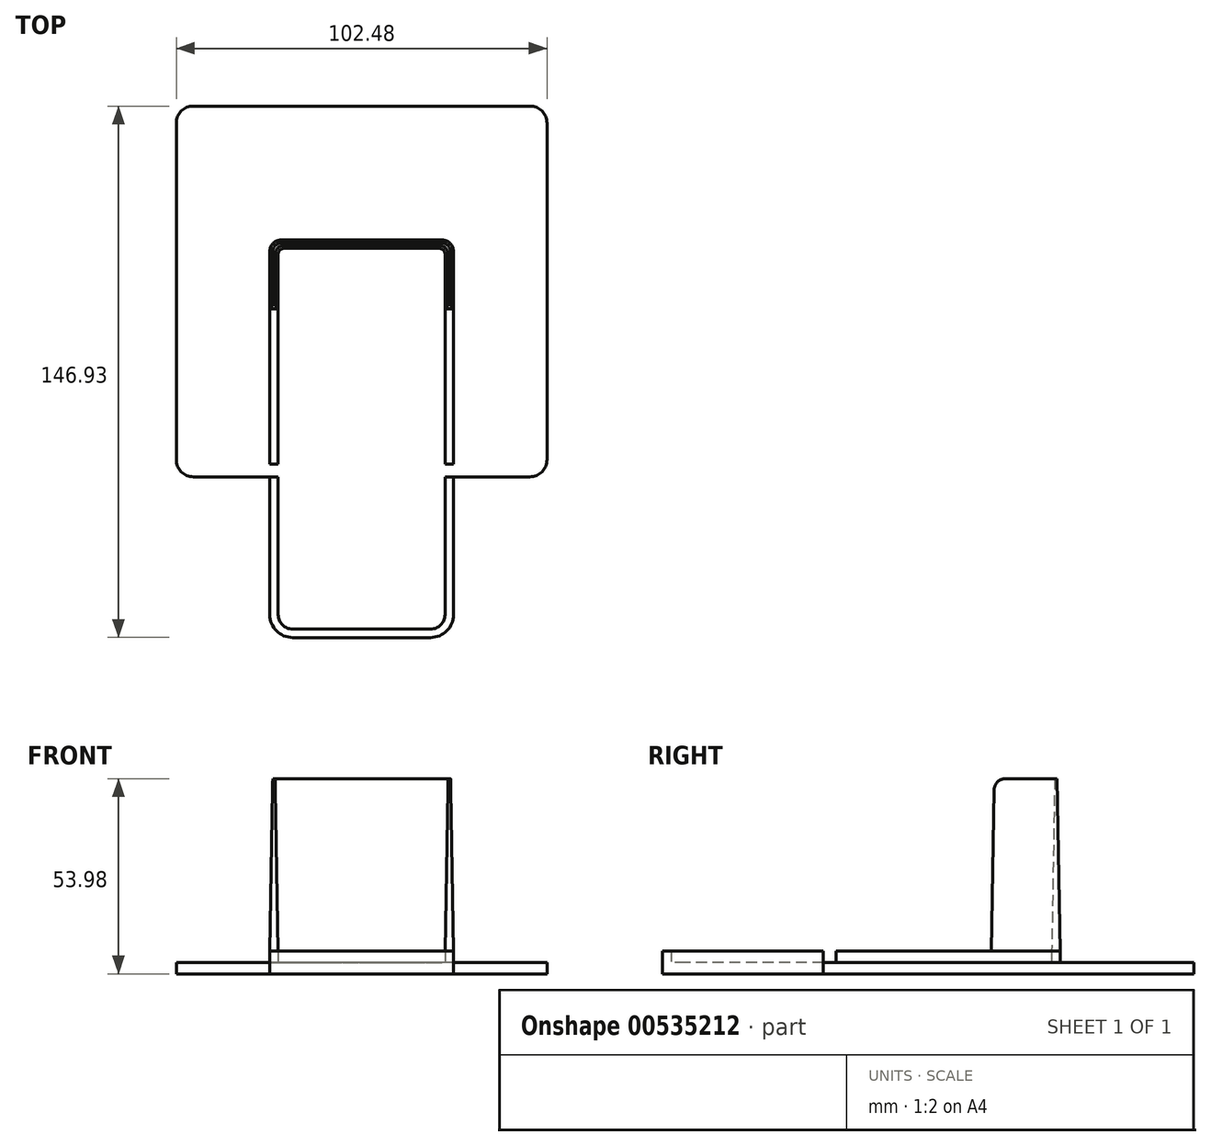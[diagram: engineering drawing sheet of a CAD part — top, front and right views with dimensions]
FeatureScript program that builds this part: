
annotation { "Feature Type Name" : "Feature", "Feature Type Description" : "" }
export const myFeature = defineFeature(function(context is Context, id is Id, definition is map)
    precondition{}
    {
        {
            var Q0;
            Q0=qCreatedBy(makeId("Top.planeOp"),FACE);
            var sketch = newSketch(context, id + "F0", { "sketchPlane" : qUnion([Q0])});
            skLineSegment(sketch, "E0.bottom", {"start": v(51.24, 51.24) * mm, "end": v(-51.24, 51.24) * mm});
            skLineSegment(sketch, "E0.top", {"start": v(51.24, -51.24) * mm, "end": v(-51.24, -51.24) * mm});
            skLineSegment(sketch, "E0.left", {"start": v(51.24, 51.24) * mm, "end": v(51.24, -51.24) * mm});
            skLineSegment(sketch, "E0.right", {"start": v(-51.24, 51.24) * mm, "end": v(-51.24, -51.24) * mm});
            skPoint(sketch, "E0.middle", {"position": v(0, 0) * mm});
            skSolve(sketch);
        }
        {
            var Q0;
            Q0=makeQuery(id+"F0.imprint","IMPRINT",FACE,{"disambiguationData":[TD([[makeQuery(id+"F0.imprint","IMPRINT",EDGE,{"derivedFrom":sQuery(id+"F0.wireOp",EDGE,"E0.bottom")}),1.0]])]});
            extrude(context, id + "F1", {"entities" : qUnion([Q0]), "depth" : 3.17 * mm, "offsetDistance" : 25.4 * mm});
        }
        {
            var Q0;
            Q0=makeQuery(id+"F1.opExtrude","CAP_FACE",FACE,{"disambiguationData":[OSD([sQuery(id+"F0.wireOp",EDGE,"E0.bottom"),sQuery(id+"F0.wireOp",EDGE,"E0.top"),sQuery(id+"F0.wireOp",EDGE,"E0.left"),sQuery(id+"F0.wireOp",EDGE,"E0.right")])],"isStart":false});
            var sketch = newSketch(context, id + "F2", { "sketchPlane" : qUnion([Q0])});
            skLineSegment(sketch, "E1.0", {"start": v(51.24, -51.24) * mm, "end": v(-51.24, -51.24) * mm});
            skLineSegment(sketch, "E2", {"start": v(-25.4, -51.24) * mm, "end": v(-25.4, -95.7) * mm});
            skLineSegment(sketch, "E3", {"start": v(-25.4, -95.7) * mm, "end": v(25.4, -95.7) * mm});
            skLineSegment(sketch, "E4", {"start": v(25.4, -95.7) * mm, "end": v(25.4, -51.24) * mm});
            skSolve(sketch);
        }
        {
            var Q0;
            {var subQ0=sQuery(id+"F2.wireOp",EDGE,"E2");Q0=makeQuery(id+"F2.imprint","IMPRINT",FACE,{"disambiguationData":[TD([[makeQuery(id+"F2.imprint","IMPRINT",EDGE,{"derivedFrom":subQ0}),1.0]])]});}
            extrude(context, id + "F3", {"entities" : qUnion([Q0]), "operationType" : NewBodyOperationType.ADD, "oppositeDirection" : true, "depth" : 3.17 * mm, "offsetDistance" : 25.4 * mm});
        }
        {
            var Q0;
            Q0=makeQuery(id+"F3.opExtrude","SWEPT_EDGE",EDGE,{"disambiguationData":[OSD([sQuery(id+"F2.wireOp",EDGE,"E3"),sQuery(id+"F2.wireOp",EDGE,"E4")])]});
            var Q1;
            Q1=makeQuery(id+"F3.opExtrude","SWEPT_EDGE",EDGE,{"disambiguationData":[OSD([sQuery(id+"F2.wireOp",EDGE,"E2"),sQuery(id+"F2.wireOp",EDGE,"E3")])]});
            fillet(context, id + "F4", {"entities" : qUnion([Q0, Q1]), "radius" : 6.32 * mm, "tangentPropagation" : true, "allowEdgeOverflow" : false});
        }
        {
            var Q0;
            Q0=makeQuery(id+"F1.opExtrude","SWEPT_EDGE",EDGE,{"disambiguationData":[OSD([sQuery(id+"F0.wireOp",EDGE,"E0.top"),sQuery(id+"F0.wireOp",EDGE,"E0.right")])]});
            var Q1;
            Q1=makeQuery(id+"F1.opExtrude","SWEPT_EDGE",EDGE,{"disambiguationData":[OSD([sQuery(id+"F0.wireOp",EDGE,"E0.top"),sQuery(id+"F0.wireOp",EDGE,"E0.left")])]});
            var Q2;
            Q2=makeQuery(id+"F1.opExtrude","SWEPT_EDGE",EDGE,{"disambiguationData":[OSD([sQuery(id+"F0.wireOp",EDGE,"E0.bottom"),sQuery(id+"F0.wireOp",EDGE,"E0.left")])]});
            var Q3;
            Q3=makeQuery(id+"F1.opExtrude","SWEPT_EDGE",EDGE,{"disambiguationData":[OSD([sQuery(id+"F0.wireOp",EDGE,"E0.bottom"),sQuery(id+"F0.wireOp",EDGE,"E0.right")])]});
            fillet(context, id + "F5", {"entities" : qUnion([Q0, Q1, Q2, Q3]), "radius" : 4.76 * mm, "tangentPropagation" : true, "allowEdgeOverflow" : false});
        }
        {
            var Q0;
            Q0=makeQuery(id+"F3.boolean.opBoolean","MERGE",FACE,{"derivedFrom":[makeQuery(id+"F1.opExtrude","CAP_FACE",FACE,{"disambiguationData":[OSD([sQuery(id+"F0.wireOp",EDGE,"E0.bottom"),sQuery(id+"F0.wireOp",EDGE,"E0.top"),sQuery(id+"F0.wireOp",EDGE,"E0.left"),sQuery(id+"F0.wireOp",EDGE,"E0.right")])],"isStart":false}),makeQuery(id+"F3.opExtrude","CAP_FACE",FACE,{"disambiguationData":[OSD([sQuery(id+"F2.wireOp",EDGE,"E1.0"),sQuery(id+"F2.wireOp",EDGE,"E2"),sQuery(id+"F2.wireOp",EDGE,"E3"),sQuery(id+"F2.wireOp",EDGE,"E4")])],"isStart":true})]});
            var sketch = newSketch(context, id + "F6", { "sketchPlane" : qUnion([Q0])});
            skLineSegment(sketch, "E5.0.0", {"start": v(25.4, -51.24) * mm, "end": v(46.48, -51.24) * mm});
            skArc(sketch, "E5.0.1", {"start": v(46.48, -51.24) * mm, "mid": v(49.85, -49.85) * mm, "end": v(51.24, -46.48) * mm});
            skLineSegment(sketch, "E5.0.2", {"start": v(51.24, -46.48) * mm, "end": v(51.24, 46.48) * mm});
            skArc(sketch, "E5.0.3", {"start": v(51.24, 46.48) * mm, "mid": v(49.85, 49.85) * mm, "end": v(46.48, 51.24) * mm});
            skLineSegment(sketch, "E5.0.4", {"start": v(46.48, 51.24) * mm, "end": v(-46.48, 51.24) * mm});
            skArc(sketch, "E5.0.5", {"start": v(-46.48, 51.24) * mm, "mid": v(-49.85, 49.85) * mm, "end": v(-51.24, 46.48) * mm});
            skLineSegment(sketch, "E5.0.6", {"start": v(-51.24, 46.48) * mm, "end": v(-51.24, -46.48) * mm});
            skArc(sketch, "E5.0.7", {"start": v(-51.24, -46.48) * mm, "mid": v(-49.85, -49.85) * mm, "end": v(-46.48, -51.24) * mm});
            skLineSegment(sketch, "E5.0.8", {"start": v(-46.48, -51.24) * mm, "end": v(-25.4, -51.24) * mm});
            skLineSegment(sketch, "E5.0.9", {"start": v(-25.4, -51.24) * mm, "end": v(-25.4, -89.37) * mm});
            skArc(sketch, "E5.0.10", {"start": v(-25.4, -89.37) * mm, "mid": v(-23.55, -93.84) * mm, "end": v(-19.08, -95.7) * mm});
            skLineSegment(sketch, "E5.0.11", {"start": v(-19.08, -95.7) * mm, "end": v(19.08, -95.7) * mm});
            skArc(sketch, "E5.0.12", {"start": v(19.08, -95.7) * mm, "mid": v(23.55, -93.84) * mm, "end": v(25.4, -89.37) * mm});
            skLineSegment(sketch, "E5.0.13", {"start": v(25.4, -89.37) * mm, "end": v(25.4, -51.24) * mm});
            skLineSegment(sketch, "E6", {"start": v(-25.4, -51.24) * mm, "end": v(-23.06, -51.24) * mm});
            skLineSegment(sketch, "E7", {"start": v(-23.06, -51.24) * mm, "end": v(-23.06, -89.37) * mm});
            skLineSegment(sketch, "E8", {"start": v(25.4, -51.24) * mm, "end": v(23.06, -51.24) * mm});
            skLineSegment(sketch, "E9", {"start": v(23.06, -51.24) * mm, "end": v(23.06, -89.37) * mm});
            skLineSegment(sketch, "E10", {"start": v(-19.08, -93.36) * mm, "end": v(19.08, -93.36) * mm});
            skArc(sketch, "E11", {"start": v(-23.06, -89.37) * mm, "mid": v(-21.9, -92.19) * mm, "end": v(-19.08, -93.36) * mm});
            skArc(sketch, "E12", {"start": v(19.08, -93.36) * mm, "mid": v(21.9, -92.19) * mm, "end": v(23.06, -89.37) * mm});
            skLineSegment(sketch, "E13", {"start": v(-25.4, -47.69) * mm, "end": v(-25.4, 11.05) * mm});
            skLineSegment(sketch, "E14", {"start": v(-22.23, 14.22) * mm, "end": v(22.23, 14.22) * mm});
            skLineSegment(sketch, "E15", {"start": v(25.4, 11.05) * mm, "end": v(25.4, -47.69) * mm});
            skLineSegment(sketch, "E16", {"start": v(25.4, -47.69) * mm, "end": v(23.06, -47.69) * mm});
            skLineSegment(sketch, "E17", {"start": v(23.06, -47.69) * mm, "end": v(23.06, 10.3) * mm});
            skLineSegment(sketch, "E18", {"start": v(21.48, 11.89) * mm, "end": v(-21.48, 11.89) * mm});
            skLineSegment(sketch, "E19", {"start": v(-23.06, 10.3) * mm, "end": v(-23.06, -47.69) * mm});
            skLineSegment(sketch, "E20", {"start": v(-23.06, -47.69) * mm, "end": v(-25.4, -47.69) * mm});
            skPoint(sketch, "E21.visualSharp", {"position": v(-25.4, 14.22) * mm});
            skArc(sketch, "E21.filletArc", {"start": v(-22.23, 14.22) * mm, "mid": v(-24.47, 13.3) * mm, "end": v(-25.4, 11.05) * mm});
            skPoint(sketch, "E22.visualSharp", {"position": v(25.4, 14.22) * mm});
            skArc(sketch, "E22.filletArc", {"start": v(25.4, 11.05) * mm, "mid": v(24.47, 13.3) * mm, "end": v(22.23, 14.22) * mm});
            skPoint(sketch, "E23.visualSharp", {"position": v(-23.06, 11.89) * mm});
            skArc(sketch, "E23.filletArc", {"start": v(-21.48, 11.89) * mm, "mid": v(-22.6, 11.42) * mm, "end": v(-23.06, 10.3) * mm});
            skPoint(sketch, "E24.visualSharp", {"position": v(23.06, 11.89) * mm});
            skArc(sketch, "E24.filletArc", {"start": v(23.06, 10.3) * mm, "mid": v(22.6, 11.42) * mm, "end": v(21.48, 11.89) * mm});
            skSolve(sketch);
        }
        {
            var Q0;
            Q0=makeQuery(id+"F6.imprint","IMPRINT",FACE,{"disambiguationData":[TD([[makeQuery(id+"F6.imprint","IMPRINT",EDGE,{"derivedFrom":sQuery(id+"F6.wireOp",EDGE,"E13")}),-1.0]])]});
            var Q1;
            Q1=makeQuery(id+"F6.imprint","IMPRINT",FACE,{"disambiguationData":[TD([[makeQuery(id+"F6.imprint","IMPRINT",EDGE,{"derivedFrom":sQuery(id+"F6.wireOp",EDGE,"E5.0.9")}),1.0]])]});
            extrude(context, id + "F7", {"entities" : qUnion([Q0, Q1]), "operationType" : NewBodyOperationType.ADD, "depth" : 3.17 * mm, "offsetDistance" : 25.4 * mm});
        }
        {
            var Q0;
            Q0=makeQuery(id+"F7.opExtrude","CAP_FACE",FACE,{"disambiguationData":[OSD([sQuery(id+"F6.wireOp",EDGE,"E13"),sQuery(id+"F6.wireOp",EDGE,"E14"),sQuery(id+"F6.wireOp",EDGE,"E15"),sQuery(id+"F6.wireOp",EDGE,"E16"),sQuery(id+"F6.wireOp",EDGE,"E17"),sQuery(id+"F6.wireOp",EDGE,"E18"),sQuery(id+"F6.wireOp",EDGE,"E19"),sQuery(id+"F6.wireOp",EDGE,"E20"),sQuery(id+"F6.wireOp",EDGE,"E21.filletArc"),sQuery(id+"F6.wireOp",EDGE,"E22.filletArc"),sQuery(id+"F6.wireOp",EDGE,"E23.filletArc"),sQuery(id+"F6.wireOp",EDGE,"E24.filletArc")])],"isStart":false});
            var sketch = newSketch(context, id + "F8", { "sketchPlane" : qUnion([Q0])});
            skArc(sketch, "E25.0.0", {"start": v(21.48, 11.89) * mm, "mid": v(22.6, 11.42) * mm, "end": v(23.06, 10.3) * mm});
            skLineSegment(sketch, "E25.0.1", {"start": v(23.06, 10.3) * mm, "end": v(23.06, -47.69) * mm});
            skLineSegment(sketch, "E25.0.2", {"start": v(23.06, -47.69) * mm, "end": v(25.4, -47.69) * mm});
            skLineSegment(sketch, "E25.0.3", {"start": v(25.4, -47.69) * mm, "end": v(25.4, 11.05) * mm});
            skArc(sketch, "E25.0.4", {"start": v(25.4, 11.05) * mm, "mid": v(24.47, 13.3) * mm, "end": v(22.23, 14.22) * mm});
            skLineSegment(sketch, "E25.0.5", {"start": v(22.23, 14.22) * mm, "end": v(-22.23, 14.22) * mm});
            skArc(sketch, "E25.0.6", {"start": v(-22.23, 14.22) * mm, "mid": v(-24.47, 13.3) * mm, "end": v(-25.4, 11.05) * mm});
            skLineSegment(sketch, "E25.0.7", {"start": v(-25.4, 11.05) * mm, "end": v(-25.4, -47.69) * mm});
            skLineSegment(sketch, "E25.0.8", {"start": v(-25.4, -47.69) * mm, "end": v(-23.06, -47.69) * mm});
            skLineSegment(sketch, "E25.0.9", {"start": v(-23.06, -47.69) * mm, "end": v(-23.06, 10.3) * mm});
            skArc(sketch, "E25.0.10", {"start": v(-23.06, 10.3) * mm, "mid": v(-22.6, 11.42) * mm, "end": v(-21.48, 11.89) * mm});
            skLineSegment(sketch, "E25.0.11", {"start": v(-21.48, 11.89) * mm, "end": v(21.48, 11.89) * mm});
            skLineSegment(sketch, "E26", {"start": v(-25.4, -4.83) * mm, "end": v(-23.06, -4.83) * mm});
            skLineSegment(sketch, "E27", {"start": v(23.06, -4.83) * mm, "end": v(25.4, -4.83) * mm});
            skSolve(sketch);
        }
        {
            var Q0;
            {var subQ5=sQuery(id+"F8.wireOp",EDGE,"E25.0.0");Q0=makeQuery(id+"F8.imprint","IMPRINT",FACE,{"disambiguationData":[TD([[makeQuery(id+"F8.imprint","IMPRINT",EDGE,{"derivedFrom":subQ5}),-1.0]])]});}
            extrude(context, id + "F9", {"entities" : qUnion([Q0]), "operationType" : NewBodyOperationType.ADD, "depth" : 47.62 * mm, "offsetDistance" : 25.4 * mm, "hasDraft" : true, "draftAngle" : 1 * degree, "draftPullDirection" : true});
        }
        {
            var Q0;
            Q0=makeQuery(id+"F9.opExtrude","CAP_EDGE",EDGE,{"disambiguationData":[OSD([sQuery(id+"F8.wireOp",EDGE,"E26")])],"isStart":false});
            var Q1;
            Q1=makeQuery(id+"F9.opExtrude","CAP_EDGE",EDGE,{"disambiguationData":[OSD([sQuery(id+"F8.wireOp",EDGE,"E27")])],"isStart":false});
            fillet(context, id + "F10", {"entities" : qUnion([Q0, Q1]), "radius" : 3.17 * mm, "tangentPropagation" : true, "allowEdgeOverflow" : false});
        }
    });
